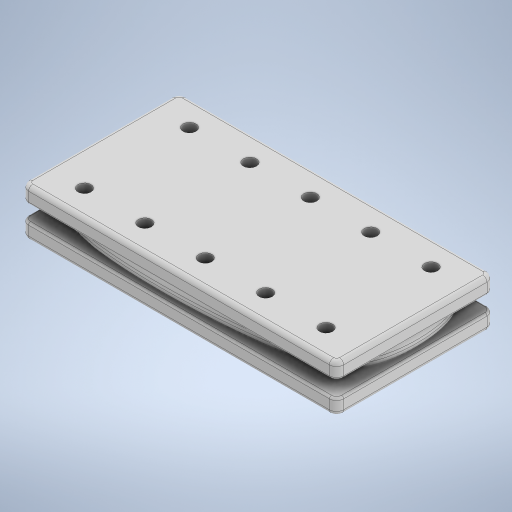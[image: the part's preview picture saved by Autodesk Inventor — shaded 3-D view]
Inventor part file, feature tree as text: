
AUTODESK INVENTOR PART (.ipt)
format: ipt  version: 2024.1 (Build 281209000, 209)  size: 463,872 bytes
history: native  units: mm
features: fillet x4, sketch x3, extrude x3, plane x1, mirror x1, other x1
ambient origin geometry x8: Origin, YZ Plane, XZ Plane, XY Plane, X Axis, Y Axis, Z Axis, Center Point
bodies: Solid1 (feature_tree)
feature tree (13):
  sketch  "Sketch1"  dims[d1=30.0mm d2=3.0mm d3=0.0mm d9=60.0mm]
  extrude  "Extrusion1"  Depth=3.0mm TaperAngle=0.0deg
  fillet  "Fillet1"  Radius=60.0mm
  plane  "Work Plane1"
  extrude  "Extrusion5"  Depth=1.36mm
  fillet  "Fillet2"  Radius=3.0mm
  fillet  "Fillet3"  Radius=0.4mm
  fillet  "Fillet4"  Radius=0.8mm
  extrude  "Extrusion6"  Depth=5.0mm
  mirror  "Mirror1"
  sketch  "Sketch5"  dims[d10=1.225mm d13=1.36mm d14=3.0mm d15=0.0mm d16=0.4mm d17=0.8mm]
  sketch  "Sketch6"  dims[d18=5.0mm d19=5.0mm d20=7.0mm d21=7.0mm d22=11.5mm d23=11.5mm d24=11.5mm d25=11.5mm d26=2.5mm d27=3.0mm d28=0.0mm]
  other  "biscuit"
